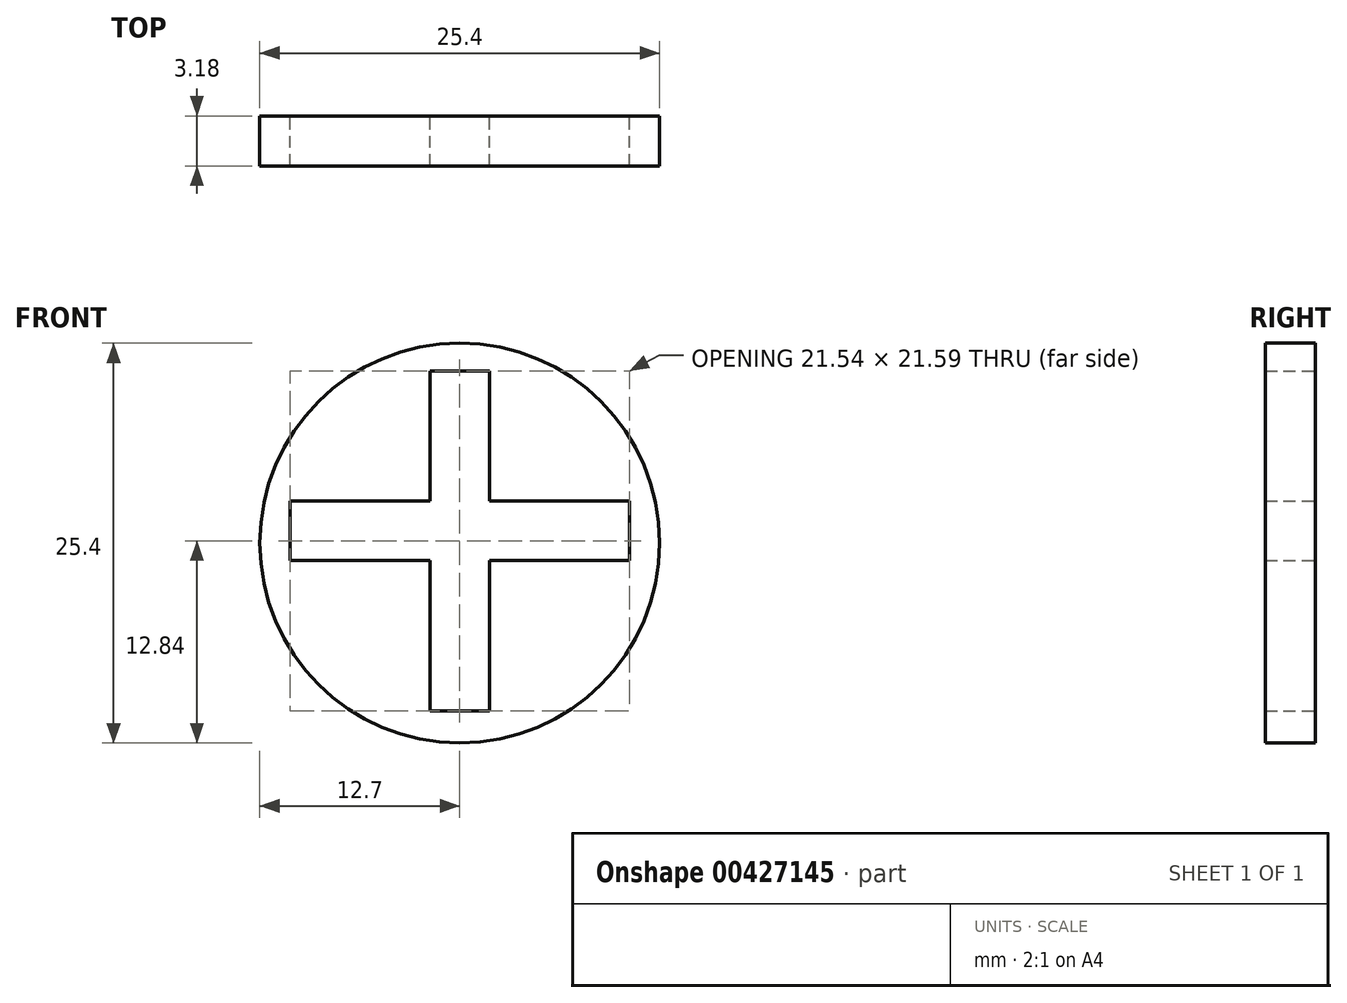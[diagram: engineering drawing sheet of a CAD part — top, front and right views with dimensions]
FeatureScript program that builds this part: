
annotation { "Feature Type Name" : "Feature", "Feature Type Description" : "" }
export const myFeature = defineFeature(function(context is Context, id is Id, definition is map)
    precondition{}
    {
        {
            var Q0;
            Q0=qCreatedBy(makeId("Front.planeOp"),FACE);
            var sketch = newSketch(context, id + "F0", { "sketchPlane" : qUnion([Q0])});
            skCircle(sketch, "E0", {"center": v(0, -0.92) * mm, "radius": 12.7 * mm});
            skLineSegment(sketch, "E1", {"start": v(-10.77, 1.76) * mm, "end": v(-10.77, -2.04) * mm});
            skLineSegment(sketch, "E2", {"start": v(-10.77, -2.04) * mm, "end": v(10.77, -2.04) * mm});
            skLineSegment(sketch, "E3", {"start": v(10.77, -2.04) * mm, "end": v(10.77, 1.76) * mm});
            skLineSegment(sketch, "E4", {"start": v(10.77, 1.76) * mm, "end": v(-10.77, 1.76) * mm});
            skLineSegment(sketch, "E5", {"start": v(-1.9, 10.01) * mm, "end": v(1.9, 10.01) * mm});
            skLineSegment(sketch, "E6", {"start": v(-1.9, 10.01) * mm, "end": v(-1.9, -11.57) * mm});
            skLineSegment(sketch, "E7", {"start": v(-1.9, -11.57) * mm, "end": v(1.9, -11.57) * mm});
            skLineSegment(sketch, "E8", {"start": v(1.9, -11.57) * mm, "end": v(1.9, 10.01) * mm});
            skSolve(sketch);
        }
        {
            var Q0;
            Q0=makeQuery(id+"F0.imprint","IMPRINT",FACE,{"disambiguationData":[TD([[makeQuery(id+"F0.imprint","IMPRINT",EDGE,{"derivedFrom":sQuery(id+"F0.wireOp",EDGE,"E0")}),1.0]])]});
            extrude(context, id + "F1", {"entities" : qUnion([Q0]), "depth" : 3.17 * mm});
        }
    });
